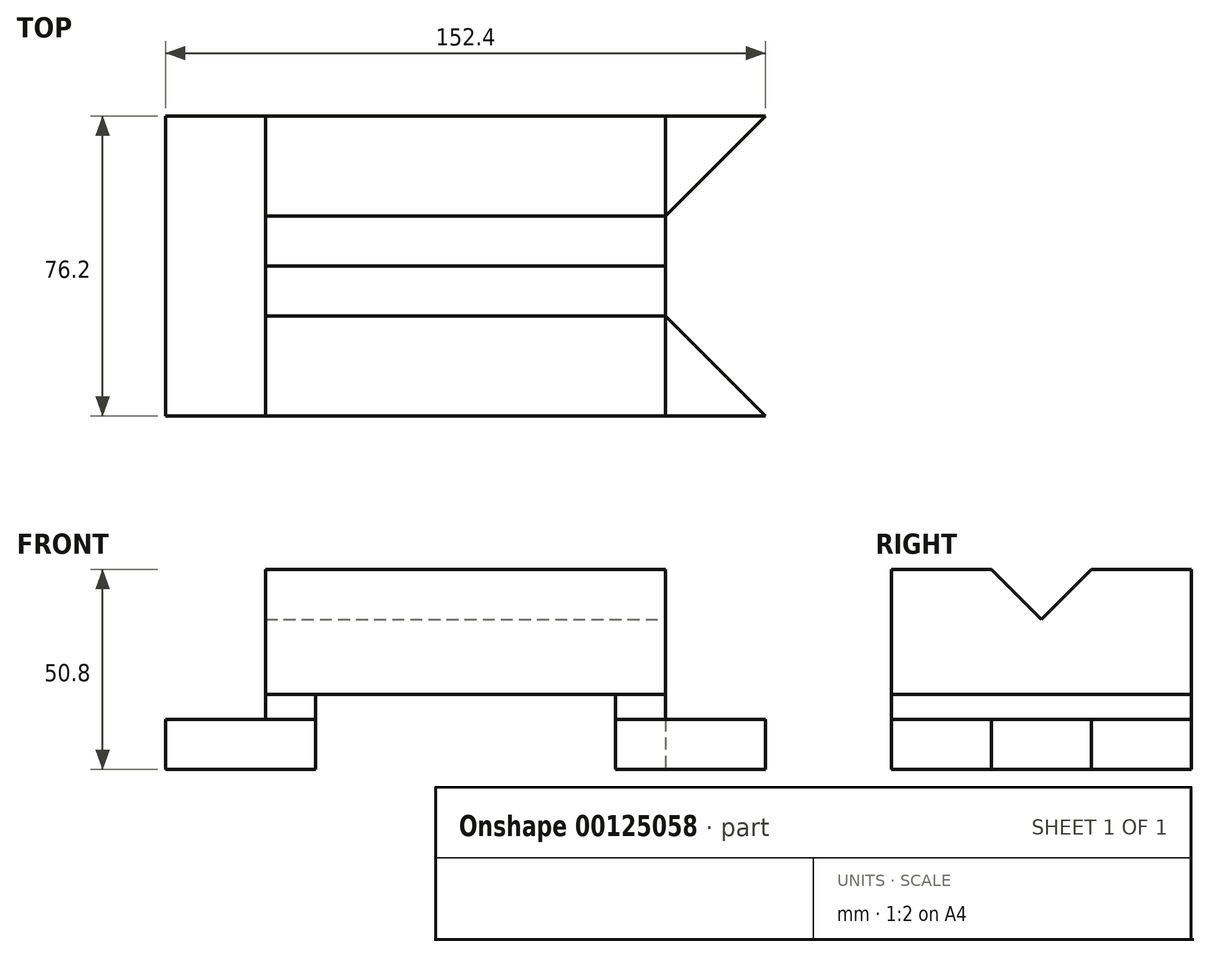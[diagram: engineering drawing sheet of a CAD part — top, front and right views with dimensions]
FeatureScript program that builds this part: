
annotation { "Feature Type Name" : "Feature", "Feature Type Description" : "" }
export const myFeature = defineFeature(function(context is Context, id is Id, definition is map)
    precondition{}
    {
        {
            var Q0;
            Q0=qCreatedBy(makeId("Top.planeOp"),FACE);
            var sketch = newSketch(context, id + "F0", { "sketchPlane" : qUnion([Q0])});
            skLineSegment(sketch, "E0.left", {"start": v(38.1, 38.1) * mm, "end": v(38.1, -38.1) * mm});
            skLineSegment(sketch, "E0.right", {"start": v(-38.1, 38.1) * mm, "end": v(-38.1, -38.1) * mm});
            skPoint(sketch, "E0.middle", {"position": v(0, 0) * mm});
            skLineSegment(sketch, "E1.bottom", {"start": v(-38.1, 38.1) * mm, "end": v(-76.2, 38.1) * mm});
            skLineSegment(sketch, "E1.top", {"start": v(-38.1, -38.1) * mm, "end": v(-76.2, -38.1) * mm});
            skLineSegment(sketch, "E1.right", {"start": v(-76.2, 38.1) * mm, "end": v(-76.2, -38.1) * mm});
            skPoint(sketch, "E2.oppositeSnap0", {"position": v(-57.15, -38.1) * mm});
            skLineSegment(sketch, "E3", {"start": v(50.8, -12.7) * mm, "end": v(76.2, -38.1) * mm});
            skLineSegment(sketch, "E4", {"start": v(76.2, 38.1) * mm, "end": v(50.8, 12.7) * mm});
            skLineSegment(sketch, "E5", {"start": v(38.1, 38.1) * mm, "end": v(76.2, 38.1) * mm});
            skLineSegment(sketch, "E6", {"start": v(38.1, -38.1) * mm, "end": v(76.2, -38.1) * mm});
            skLineSegment(sketch, "E7", {"start": v(50.8, -12.7) * mm, "end": v(50.8, 12.7) * mm});
            skSolve(sketch);
        }
        {
            var Q0;
            Q0 = qSketchRegion(id + "F0", true);
            extrude(context, id + "F1", {"entities" : qUnion([Q0]), "depth" : 12.7 * mm});
        }
        {
            var Q0;
            Q0=makeQuery(id+"F1.opExtrude","CAP_FACE",FACE,{"disambiguationData":[OSD([sQuery(id+"F0.wireOp",EDGE,"E0.left"),sQuery(id+"F0.wireOp",EDGE,"E3"),sQuery(id+"F0.wireOp",EDGE,"E4"),sQuery(id+"F0.wireOp",EDGE,"E5"),sQuery(id+"F0.wireOp",EDGE,"E6"),sQuery(id+"F0.wireOp",EDGE,"E7")])],"isStart":false});
            var sketch = newSketch(context, id + "F2", { "sketchPlane" : qUnion([Q0])});
            skPoint(sketch, "E8.oppositeSnap0", {"position": v(50.8, 0) * mm});
            skLineSegment(sketch, "E8.bottom", {"start": v(38.1, 38.1) * mm, "end": v(50.8, 38.1) * mm});
            skLineSegment(sketch, "E8.top", {"start": v(38.1, -38.1) * mm, "end": v(50.8, -38.1) * mm});
            skLineSegment(sketch, "E8.left", {"start": v(38.1, 38.1) * mm, "end": v(38.1, -38.1) * mm});
            skLineSegment(sketch, "E8.right", {"start": v(50.8, 38.1) * mm, "end": v(50.8, -38.1) * mm});
            skLineSegment(sketch, "E9.right", {"start": v(-38.1, 38.1) * mm, "end": v(-38.1, -38.1) * mm});
            skPoint(sketch, "E9.middle", {"position": v(0, 0) * mm});
            skLineSegment(sketch, "E10.bottom", {"start": v(-38.1, 38.1) * mm, "end": v(-50.8, 38.1) * mm});
            skLineSegment(sketch, "E10.top", {"start": v(-38.1, -38.1) * mm, "end": v(-50.8, -38.1) * mm});
            skLineSegment(sketch, "E10.right", {"start": v(-50.8, 38.1) * mm, "end": v(-50.8, -38.1) * mm});
            skSolve(sketch);
        }
        {
            var Q0;
            Q0 = qSketchRegion(id + "F2", true);
            extrude(context, id + "F3", {"entities" : qUnion([Q0]), "depth" : 6.35 * mm});
        }
        {
            var Q0;
            Q0=makeQuery(id+"F3.opExtrude","CAP_FACE",FACE,{"disambiguationData":[OSD([sQuery(id+"F2.wireOp",EDGE,"E10.bottom"),sQuery(id+"F2.wireOp",EDGE,"E10.top"),sQuery(id+"F2.wireOp",EDGE,"E9.right"),sQuery(id+"F2.wireOp",EDGE,"E10.right")])],"isStart":false});
            var sketch = newSketch(context, id + "F4", { "sketchPlane" : qUnion([Q0])});
            skLineSegment(sketch, "E11.bottom", {"start": v(-50.8, 38.1) * mm, "end": v(50.8, 38.1) * mm});
            skLineSegment(sketch, "E11.top", {"start": v(-50.8, -38.1) * mm, "end": v(50.8, -38.1) * mm});
            skLineSegment(sketch, "E11.left", {"start": v(-50.8, 38.1) * mm, "end": v(-50.8, -38.1) * mm});
            skLineSegment(sketch, "E11.right", {"start": v(50.8, 38.1) * mm, "end": v(50.8, -38.1) * mm});
            skSolve(sketch);
        }
        {
            var Q0;
            Q0 = qSketchRegion(id + "F4", true);
            extrude(context, id + "F5", {"entities" : qUnion([Q0]), "depth" : 31.75 * mm});
        }
        {
            var Q0;
            Q0=makeQuery(id+"F5.opExtrude","SWEPT_FACE",FACE,{"disambiguationData":[OSD([sQuery(id+"F4.wireOp",EDGE,"E11.right")])]});
            var sketch = newSketch(context, id + "F6", { "sketchPlane" : qUnion([Q0])});
            skLineSegment(sketch, "E12", {"start": v(0, 38.1) * mm, "end": v(-12.7, 50.8) * mm});
            skLineSegment(sketch, "E13", {"start": v(12.7, 50.8) * mm, "end": v(0, 38.1) * mm});
            skLineSegment(sketch, "E14", {"start": v(-12.7, 50.8) * mm, "end": v(12.7, 50.8) * mm});
            skSolve(sketch);
        }
        {
            var Q0;
            Q0 = qSketchRegion(id + "F6", true);
            extrude(context, id + "F7", {"entities" : qUnion([Q0]), "operationType" : NewBodyOperationType.REMOVE, "endBound" : BoundingType.THROUGH_ALL, "oppositeDirection" : true, "depth" : 25.4 * mm});
        }
    });
